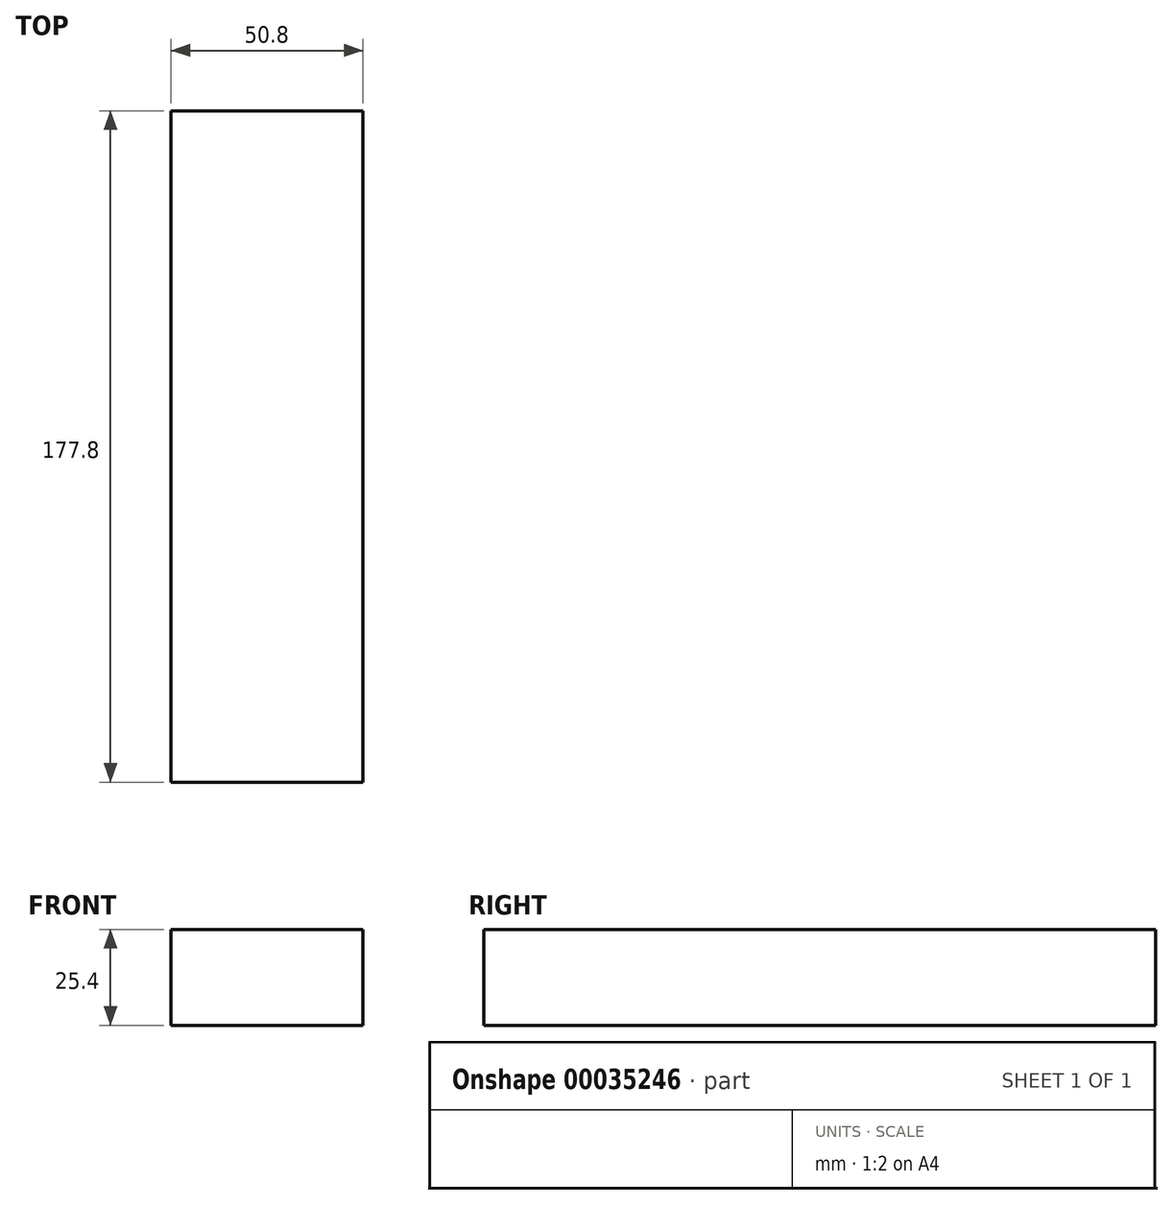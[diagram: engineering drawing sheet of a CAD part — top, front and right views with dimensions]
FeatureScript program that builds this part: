
annotation { "Feature Type Name" : "Feature", "Feature Type Description" : "" }
export const myFeature = defineFeature(function(context is Context, id is Id, definition is map)
    precondition{}
    {
        {
            var Q0;
            Q0=qCreatedBy(makeId("Top.planeOp"),FACE);
            var sketch = newSketch(context, id + "F0", { "sketchPlane" : qUnion([Q0])});
            skLineSegment(sketch, "E0.rect.bottom", {"start": v(25.4, -88.9) * mm, "end": v(-25.4, -88.9) * mm});
            skLineSegment(sketch, "E0.rect.top", {"start": v(25.4, 88.9) * mm, "end": v(-25.4, 88.9) * mm});
            skLineSegment(sketch, "E0.rect.left", {"start": v(25.4, -88.9) * mm, "end": v(25.4, 88.9) * mm});
            skLineSegment(sketch, "E0.rect.right", {"start": v(-25.4, -88.9) * mm, "end": v(-25.4, 88.9) * mm});
            skPoint(sketch, "E0.rect.middle", {"position": v(0, 0) * mm});
            skSolve(sketch);
        }
        {
            var Q0;
            Q0=makeQuery(id+"F0.imprint","IMPRINT",FACE,{"disambiguationData":[TD([[makeQuery(id+"F0.imprint","IMPRINT",EDGE,{"derivedFrom":sQuery(id+"F0.wireOp",EDGE,"E0.rect.bottom")}),-1.0]])]});
            extrude(context, id + "F1", {"entities" : qUnion([Q0]), "depth" : 25.4 * mm});
        }
    });
